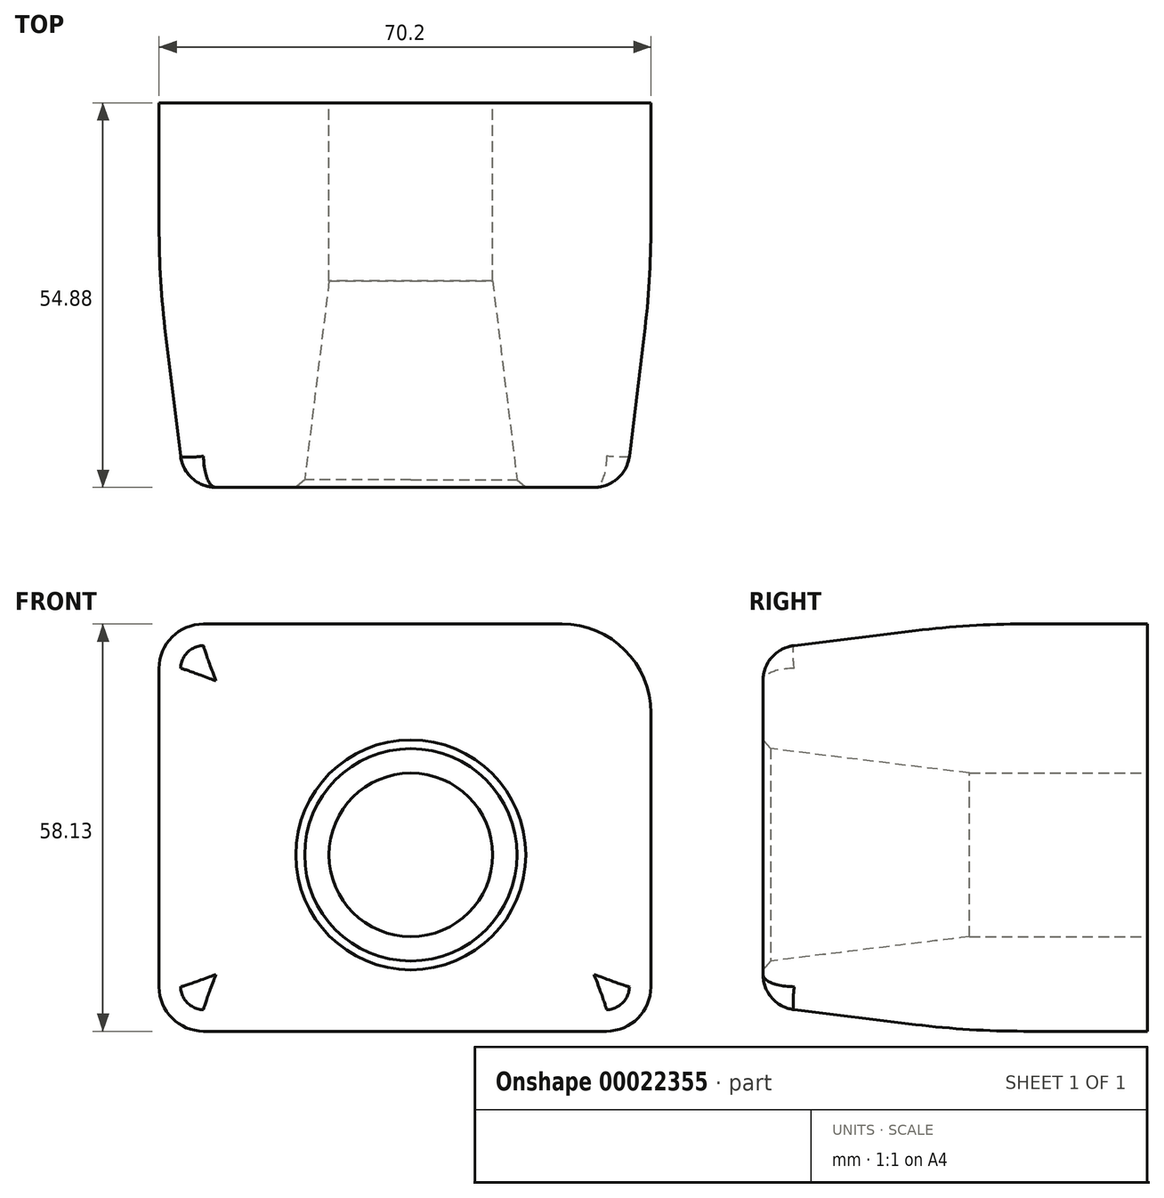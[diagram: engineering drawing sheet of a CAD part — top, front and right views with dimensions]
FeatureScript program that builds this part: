
annotation { "Feature Type Name" : "Feature", "Feature Type Description" : "" }
export const myFeature = defineFeature(function(context is Context, id is Id, definition is map)
    precondition{}
    {
        {
            var Q0;
            Q0=qCreatedBy(makeId("Front.planeOp"),FACE);
            var sketch = newSketch(context, id + "F0", { "sketchPlane" : qUnion([Q0])});
            skLineSegment(sketch, "E0.bottom", {"start": v(-29.58, 32.95) * mm, "end": v(21.57, 32.95) * mm});
            skLineSegment(sketch, "E0.top", {"start": v(-29.58, -25.18) * mm, "end": v(27.92, -25.18) * mm});
            skLineSegment(sketch, "E0.left", {"start": v(-35.93, 26.6) * mm, "end": v(-35.93, -18.83) * mm});
            skLineSegment(sketch, "E0.right", {"start": v(34.27, 20.25) * mm, "end": v(34.27, -18.83) * mm});
            skPoint(sketch, "E1.visualSharp", {"position": v(-35.93, 32.95) * mm});
            skArc(sketch, "E1.filletArc", {"start": v(-29.58, 32.95) * mm, "mid": v(-34.07, 31.09) * mm, "end": v(-35.93, 26.6) * mm});
            skPoint(sketch, "E2.visualSharp", {"position": v(-35.93, -25.18) * mm});
            skArc(sketch, "E2.filletArc", {"start": v(-35.93, -18.83) * mm, "mid": v(-34.07, -23.32) * mm, "end": v(-29.58, -25.18) * mm});
            skPoint(sketch, "E3.visualSharp", {"position": v(34.27, -25.18) * mm});
            skArc(sketch, "E3.filletArc", {"start": v(27.92, -25.18) * mm, "mid": v(32.41, -23.32) * mm, "end": v(34.27, -18.83) * mm});
            skPoint(sketch, "E4.visualSharp", {"position": v(34.27, 32.95) * mm});
            skArc(sketch, "E4.filletArc", {"start": v(34.27, 20.25) * mm, "mid": v(30.55, 29.23) * mm, "end": v(21.57, 32.95) * mm});
            skCircle(sketch, "E5", {"center": v(0, 0) * mm, "radius": 11.67 * mm});
            skSolve(sketch);
        }
        {
            var Q0;
            Q0=makeQuery(id+"F0.imprint","IMPRINT",FACE,{"disambiguationData":[TD([[makeQuery(id+"F0.imprint","IMPRINT",EDGE,{"derivedFrom":sQuery(id+"F0.wireOp",EDGE,"E0.bottom")}),-1.0]])]});
            extrude(context, id + "F1", {"entities" : qUnion([Q0]), "depth" : 29.48 * mm, "hasDraft" : true, "draftAngle" : 7 * degree, "draftPullDirection" : true, "hasSecondDirection" : true, "secondDirectionOppositeDirection" : true, "secondDirectionDepth" : 25.4 * mm});
        }
        {
            var Q0;
            Q0=makeQuery(id+"F1.opExtrude","CAP_EDGE",EDGE,{"disambiguationData":[OSD([sQuery(id+"F0.wireOp",EDGE,"E0.top")])],"isStart":false});
            fillet(context, id + "F2", {"entities" : qUnion([Q0]), "radius" : 5.08 * mm, "tangentPropagation" : true, "allowEdgeOverflow" : false});
        }
        {
            var Q0;
            Q0=makeQuery(id+"F1.opExtrude","CAP_EDGE",EDGE,{"disambiguationData":[OSD([sQuery(id+"F0.wireOp",EDGE,"E5")])],"isStart":false});
            chamfer(context, id + "F3", {"entities" : qUnion([Q0]), "width" : 1.27 * mm, "tangentPropagation" : true});
        }
        {
            var Q0;
            {var subQ0=makeQuery(id+"F1.opExtrude","SWEPT_FACE",FACE,{"disambiguationData":[OSD([sQuery(id+"F0.wireOp",EDGE,"E4.filletArc")])]});Q0=makeQuery(id+"F1.*.booleanUnion.opBoolean","MERGE",EDGE,{"derivedFrom":[makeQuery(id+"F1.*.split.splitOp","SPLIT_SURFACE_INTERSECT",EDGE,{"derivedFrom":[subQ0]}),makeQuery(id+"F1.*.split.splitOp","SPLIT_SURFACE_INTERSECT",EDGE,{"derivedFrom":[subQ0],"isFromBackBody":true})]});}
            var Q1;
            {var subQ0=makeQuery(id+"F1.opExtrude","SWEPT_FACE",FACE,{"disambiguationData":[OSD([sQuery(id+"F0.wireOp",EDGE,"E0.right")])]});Q1=makeQuery(id+"F1.*.booleanUnion.opBoolean","MERGE",EDGE,{"derivedFrom":[makeQuery(id+"F1.*.split.splitOp","SPLIT_SURFACE_INTERSECT",EDGE,{"derivedFrom":[subQ0]}),makeQuery(id+"F1.*.split.splitOp","SPLIT_SURFACE_INTERSECT",EDGE,{"derivedFrom":[subQ0],"isFromBackBody":true})]});}
            var Q2;
            {var subQ0=makeQuery(id+"F1.opExtrude","SWEPT_FACE",FACE,{"disambiguationData":[OSD([sQuery(id+"F0.wireOp",EDGE,"E3.filletArc")])]});Q2=makeQuery(id+"F1.*.booleanUnion.opBoolean","MERGE",EDGE,{"derivedFrom":[makeQuery(id+"F1.*.split.splitOp","SPLIT_SURFACE_INTERSECT",EDGE,{"derivedFrom":[subQ0]}),makeQuery(id+"F1.*.split.splitOp","SPLIT_SURFACE_INTERSECT",EDGE,{"derivedFrom":[subQ0],"isFromBackBody":true})]});}
            var Q3;
            {var subQ0=makeQuery(id+"F1.opExtrude","SWEPT_FACE",FACE,{"disambiguationData":[OSD([sQuery(id+"F0.wireOp",EDGE,"E0.bottom")])]});Q3=makeQuery(id+"F1.*.booleanUnion.opBoolean","MERGE",EDGE,{"derivedFrom":[makeQuery(id+"F1.*.split.splitOp","SPLIT_SURFACE_INTERSECT",EDGE,{"derivedFrom":[subQ0]}),makeQuery(id+"F1.*.split.splitOp","SPLIT_SURFACE_INTERSECT",EDGE,{"derivedFrom":[subQ0],"isFromBackBody":true})]});}
            var Q4;
            {var subQ0=makeQuery(id+"F1.opExtrude","SWEPT_FACE",FACE,{"disambiguationData":[OSD([sQuery(id+"F0.wireOp",EDGE,"E1.filletArc")])]});Q4=makeQuery(id+"F1.*.booleanUnion.opBoolean","MERGE",EDGE,{"derivedFrom":[makeQuery(id+"F1.*.split.splitOp","SPLIT_SURFACE_INTERSECT",EDGE,{"derivedFrom":[subQ0]}),makeQuery(id+"F1.*.split.splitOp","SPLIT_SURFACE_INTERSECT",EDGE,{"derivedFrom":[subQ0],"isFromBackBody":true})]});}
            var Q5;
            {var subQ0=makeQuery(id+"F1.opExtrude","SWEPT_FACE",FACE,{"disambiguationData":[OSD([sQuery(id+"F0.wireOp",EDGE,"E0.left")])]});Q5=makeQuery(id+"F1.*.booleanUnion.opBoolean","MERGE",EDGE,{"derivedFrom":[makeQuery(id+"F1.*.split.splitOp","SPLIT_SURFACE_INTERSECT",EDGE,{"derivedFrom":[subQ0]}),makeQuery(id+"F1.*.split.splitOp","SPLIT_SURFACE_INTERSECT",EDGE,{"derivedFrom":[subQ0],"isFromBackBody":true})]});}
            var Q6;
            {var subQ0=makeQuery(id+"F1.opExtrude","SWEPT_FACE",FACE,{"disambiguationData":[OSD([sQuery(id+"F0.wireOp",EDGE,"E2.filletArc")])]});Q6=makeQuery(id+"F1.*.booleanUnion.opBoolean","MERGE",EDGE,{"derivedFrom":[makeQuery(id+"F1.*.split.splitOp","SPLIT_SURFACE_INTERSECT",EDGE,{"derivedFrom":[subQ0]}),makeQuery(id+"F1.*.split.splitOp","SPLIT_SURFACE_INTERSECT",EDGE,{"derivedFrom":[subQ0],"isFromBackBody":true})]});}
            var Q7;
            {var subQ0=makeQuery(id+"F1.opExtrude","SWEPT_FACE",FACE,{"disambiguationData":[OSD([sQuery(id+"F0.wireOp",EDGE,"E0.top")])]});Q7=makeQuery(id+"F1.*.booleanUnion.opBoolean","MERGE",EDGE,{"derivedFrom":[makeQuery(id+"F1.*.split.splitOp","SPLIT_SURFACE_INTERSECT",EDGE,{"derivedFrom":[subQ0]}),makeQuery(id+"F1.*.split.splitOp","SPLIT_SURFACE_INTERSECT",EDGE,{"derivedFrom":[subQ0],"isFromBackBody":true})]});}
            fillet(context, id + "F4", {"entities" : qUnion([Q0, Q1, Q2, Q3, Q4, Q5, Q6, Q7]), "radius" : 127 * mm, "tangentPropagation" : true, "allowEdgeOverflow" : false});
        }
    });
